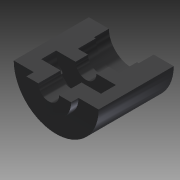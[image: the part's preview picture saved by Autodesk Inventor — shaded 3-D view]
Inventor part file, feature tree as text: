
AUTODESK INVENTOR PART (.ipt)
format: ipt  version: 2013 (Build 170138000, 138)  size: 143,360 bytes
history: native  units: in
note: dims shown in document units (in); Inventor stores cm internally (conversion verified against a paired STEP export)
features: sketch x2, chamfer x1, other x1, split x1, extrude x1, revolve x1, imported_body x1, projected_geometry x1
ambient origin geometry x8: Origin, YZ Plane, XZ Plane, XY Plane, X Axis, Y Axis, Z Axis, Center Point
feature tree (9):
  chamfer  "Chamfer2"  Distance=0.0625in
  other  "217-2428-011 Rev2 1"
  split  "Split1"
  extrude  "Extrusion1"  Depth=0.1875in
  revolve  "Revolution1"  [1 undecoded]
  imported_body  "Base1"
  sketch  "Sketch1"  dims[d0=0.375in d2=0.0625in d3=0.0in]
  sketch  "Sketch2"  dims[d4=0.125in d8=0.1875in d9=0.25in d10=90.0deg]
  projected_geometry  "Project Cut Edges1"
note: 1 required parameter value undecoded (feature->parameter linkage not recoverable at this tier; creation-order binding heuristic only, values carry confidence <= 0.55)
